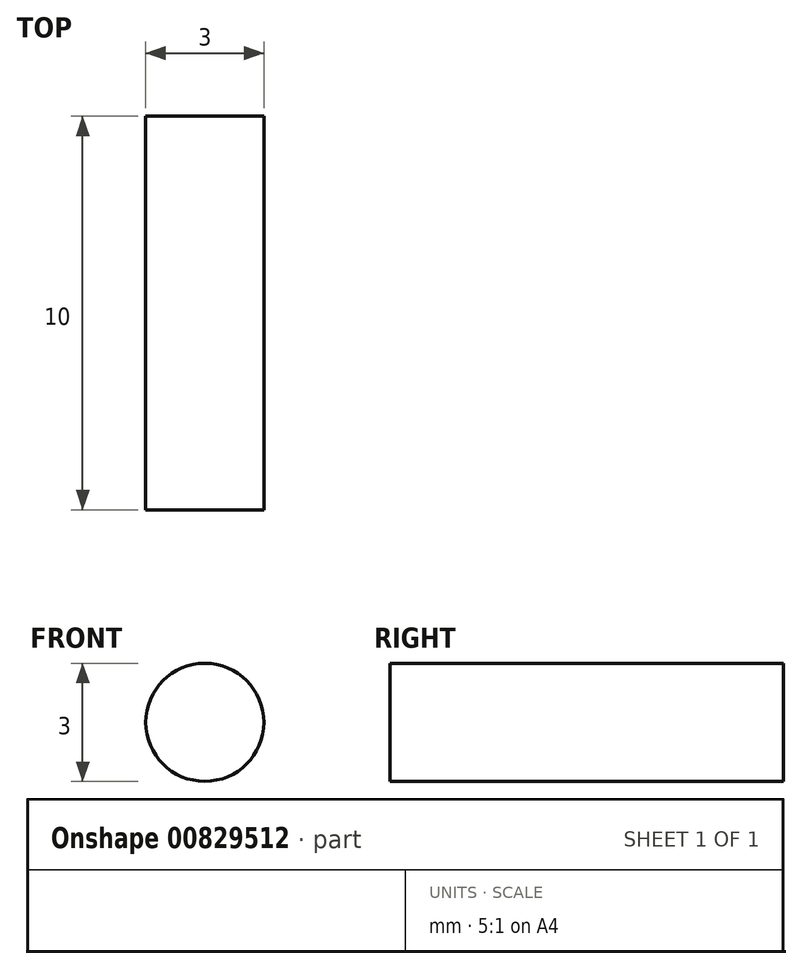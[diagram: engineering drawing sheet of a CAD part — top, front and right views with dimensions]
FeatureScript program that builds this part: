
annotation { "Feature Type Name" : "Feature", "Feature Type Description" : "" }
export const myFeature = defineFeature(function(context is Context, id is Id, definition is map)
    precondition{}
    {
        {
            var Q0;
            Q0=qCreatedBy(makeId("Front.planeOp"),FACE);
            var sketch = newSketch(context, id + "F0", { "sketchPlane" : qUnion([Q0])});
            skCircle(sketch, "E0", {"center": v(0, 0) * mm, "radius": 1.5 * mm});
            skSolve(sketch);
        }
        {
            var Q0;
            Q0 = qSketchRegion(id + "F0", true);
            extrude(context, id + "F1", {"entities" : qUnion([Q0]), "endBound" : BoundingType.SYMMETRIC, "depth" : 10 * mm, "offsetDistance" : 25 * mm});
        }
    });
